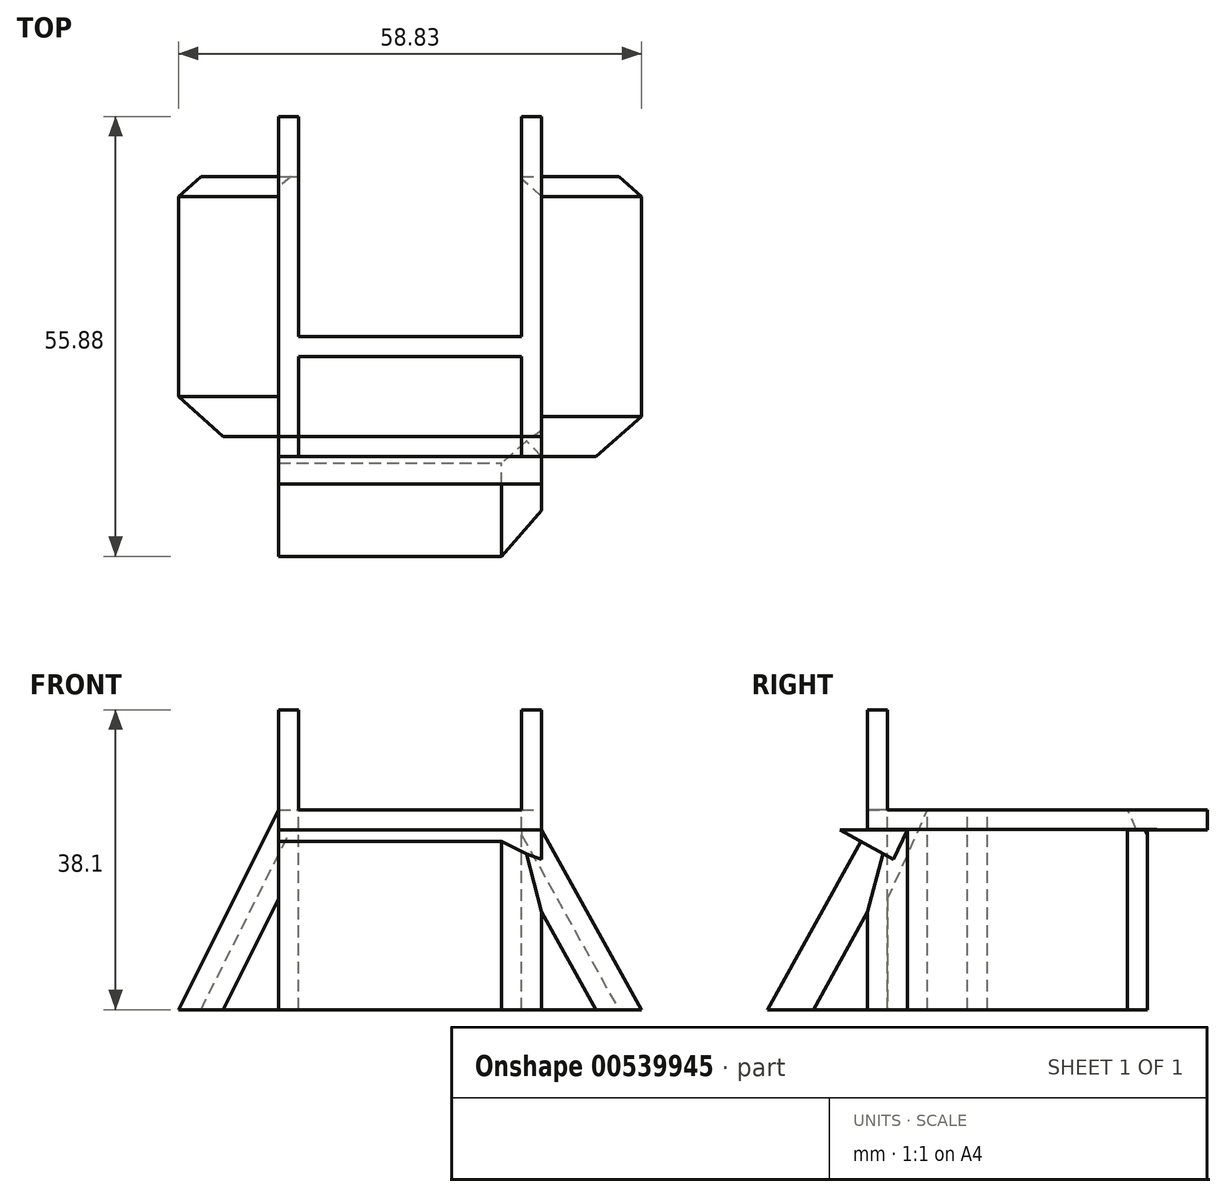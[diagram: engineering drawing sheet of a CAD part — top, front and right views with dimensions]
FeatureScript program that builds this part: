
annotation { "Feature Type Name" : "Feature", "Feature Type Description" : "" }
export const myFeature = defineFeature(function(context is Context, id is Id, definition is map)
    precondition{}
    {
        {
            var Q0;
            Q0=qCreatedBy(makeId("Front.planeOp"),FACE);
            var sketch = newSketch(context, id + "F0", { "sketchPlane" : qUnion([Q0])});
            skLineSegment(sketch, "E0.bottom", {"start": v(0, 0) * mm, "end": v(2.54, 0) * mm});
            skLineSegment(sketch, "E0.top", {"start": v(0, 2.54) * mm, "end": v(2.54, 2.54) * mm});
            skLineSegment(sketch, "E0.left", {"start": v(0, 0) * mm, "end": v(0, 2.54) * mm});
            skLineSegment(sketch, "E0.right", {"start": v(2.54, 0) * mm, "end": v(2.54, 2.54) * mm});
            skLineSegment(sketch, "E1", {"start": v(2.54, 0) * mm, "end": v(30.89, 0) * mm, "construction": true});
            skLineSegment(sketch, "E2.bottom", {"start": v(30.89, 0) * mm, "end": v(33.43, 0) * mm});
            skLineSegment(sketch, "E2.top", {"start": v(30.89, 2.54) * mm, "end": v(33.43, 2.54) * mm});
            skLineSegment(sketch, "E2.left", {"start": v(30.89, 0) * mm, "end": v(30.89, 2.54) * mm});
            skLineSegment(sketch, "E2.right", {"start": v(33.43, 0) * mm, "end": v(33.43, 2.54) * mm});
            skLineSegment(sketch, "E3.bottom", {"start": v(0, 0) * mm, "end": v(33.43, 0) * mm});
            skLineSegment(sketch, "E3.top", {"start": v(0, 2.54) * mm, "end": v(33.43, 2.54) * mm});
            skSolve(sketch);
        }
        {
            var Q0;
            {var subQ0=sQuery(id+"F0.wireOp",EDGE,"E0.right");Q0=makeQuery(id+"F0.imprint","IMPRINT",FACE,{"disambiguationData":[TD([[makeQuery(id+"F0.imprint","IMPRINT",EDGE,{"derivedFrom":subQ0}),-1.0]])]});}
            var Q1;
            {var subQ0=sQuery(id+"F0.wireOp",EDGE,"E0.right");Q1=makeQuery(id+"F0.imprint","IMPRINT",FACE,{"disambiguationData":[TD([[makeQuery(id+"F0.imprint","IMPRINT",EDGE,{"derivedFrom":subQ0}),1.0]])]});}
            var Q2;
            {var subQ0=sQuery(id+"F0.wireOp",EDGE,"E2.left");Q2=makeQuery(id+"F0.imprint","IMPRINT",FACE,{"disambiguationData":[TD([[makeQuery(id+"F0.imprint","IMPRINT",EDGE,{"derivedFrom":subQ0}),-1.0]])]});}
            extrude(context, id + "F1", {"entities" : qUnion([Q0, Q1, Q2]), "depth" : 43.18 * mm, "offsetDistance" : 25.4 * mm});
        }
        {
            var Q0;
            Q0=makeQuery(id+"F1.opExtrude","SWEPT_FACE",FACE,{"disambiguationData":[OSD([sQuery(id+"F0.wireOp",EDGE,"E3.top")])]});
            var sketch = newSketch(context, id + "F2", { "sketchPlane" : qUnion([Q0])});
            skLineSegment(sketch, "E4", {"start": v(0, 0) * mm, "end": v(2.54, 0) * mm});
            skLineSegment(sketch, "E5", {"start": v(2.54, 0) * mm, "end": v(30.89, 0) * mm, "construction": true});
            skLineSegment(sketch, "E6", {"start": v(30.89, 0) * mm, "end": v(33.43, 0) * mm});
            skLineSegment(sketch, "E7.bottom", {"start": v(2.54, 0) * mm, "end": v(30.89, 0) * mm});
            skLineSegment(sketch, "E7.top", {"start": v(2.54, -40.64) * mm, "end": v(30.89, -40.64) * mm});
            skLineSegment(sketch, "E7.left", {"start": v(2.54, 0) * mm, "end": v(2.54, -40.64) * mm});
            skLineSegment(sketch, "E7.right", {"start": v(30.89, 0) * mm, "end": v(30.89, -40.64) * mm});
            skLineSegment(sketch, "E8.bottom", {"start": v(2.54, -40.64) * mm, "end": v(0, -40.64) * mm});
            skLineSegment(sketch, "E8.top", {"start": v(2.54, -43.18) * mm, "end": v(0, -43.18) * mm});
            skLineSegment(sketch, "E8.left", {"start": v(2.54, -40.64) * mm, "end": v(2.54, -43.18) * mm});
            skLineSegment(sketch, "E8.right", {"start": v(0, -40.64) * mm, "end": v(0, -43.18) * mm});
            skLineSegment(sketch, "E9.bottom", {"start": v(30.89, -40.64) * mm, "end": v(33.43, -40.64) * mm});
            skLineSegment(sketch, "E9.top", {"start": v(30.89, -43.18) * mm, "end": v(33.43, -43.18) * mm});
            skLineSegment(sketch, "E9.left", {"start": v(30.89, -40.64) * mm, "end": v(30.89, -43.18) * mm});
            skLineSegment(sketch, "E9.right", {"start": v(33.43, -40.64) * mm, "end": v(33.43, -43.18) * mm});
            skLineSegment(sketch, "E10", {"start": v(2.54, 0) * mm, "end": v(2.54, -30.48) * mm, "construction": true});
            skLineSegment(sketch, "E11", {"start": v(2.54, -30.48) * mm, "end": v(30.89, -30.48) * mm});
            skLineSegment(sketch, "E12", {"start": v(2.54, -30.48) * mm, "end": v(2.54, -27.94) * mm});
            skLineSegment(sketch, "E13", {"start": v(2.54, -27.94) * mm, "end": v(30.89, -27.94) * mm});
            skLineSegment(sketch, "E14", {"start": v(0, 0) * mm, "end": v(0, -7.62) * mm});
            skLineSegment(sketch, "E15", {"start": v(0, -7.62) * mm, "end": v(2.54, -7.62) * mm});
            skLineSegment(sketch, "E16", {"start": v(33.43, 0) * mm, "end": v(33.43, -7.62) * mm});
            skLineSegment(sketch, "E17", {"start": v(33.43, -7.62) * mm, "end": v(30.89, -7.62) * mm});
            skSolve(sketch);
        }
        {
            var Q0;
            Q0=makeQuery(id+"F2.imprint","IMPRINT",FACE,{"disambiguationData":[TD([[makeQuery(id+"F2.imprint","IMPRINT",EDGE,{"derivedFrom":sQuery(id+"F2.wireOp",EDGE,"E7.bottom")}),-1.0]])]});
            var Q1;
            {var subQ0=sQuery(id+"F2.wireOp",EDGE,"E7.top");Q1=makeQuery(id+"F2.imprint","IMPRINT",FACE,{"disambiguationData":[TD([[makeQuery(id+"F2.imprint","IMPRINT",EDGE,{"derivedFrom":subQ0}),1.0]])]});}
            extrude(context, id + "F3", {"entities" : qUnion([Q0, Q1]), "operationType" : NewBodyOperationType.REMOVE, "oppositeDirection" : true, "depth" : 2.54 * mm, "offsetDistance" : 25.4 * mm});
        }
        {
            var Q0;
            Q0=makeQuery(id+"F2.imprint","IMPRINT",FACE,{"disambiguationData":[TD([[makeQuery(id+"F2.imprint","IMPRINT",EDGE,{"derivedFrom":sQuery(id+"F2.wireOp",EDGE,"E8.bottom")}),1.0]])]});
            var Q1;
            Q1=makeQuery(id+"F2.imprint","IMPRINT",FACE,{"disambiguationData":[TD([[makeQuery(id+"F2.imprint","IMPRINT",EDGE,{"derivedFrom":sQuery(id+"F2.wireOp",EDGE,"E9.bottom")}),-1.0]])]});
            extrude(context, id + "F4", {"entities" : qUnion([Q0, Q1]), "operationType" : NewBodyOperationType.ADD, "depth" : 12.7 * mm, "offsetDistance" : 25.4 * mm});
        }
        {
            var Q0;
            {var subQ0=sQuery(id+"F2.wireOp",EDGE,"E8.bottom");Q0=makeQuery(id+"F2.imprint","IMPRINT",FACE,{"disambiguationData":[TD([[makeQuery(id+"F2.imprint","IMPRINT",EDGE,{"derivedFrom":subQ0}),-1.0]])]});}
            var Q1;
            {var subQ0=sQuery(id+"F2.wireOp",EDGE,"E9.bottom");Q1=makeQuery(id+"F2.imprint","IMPRINT",FACE,{"disambiguationData":[TD([[makeQuery(id+"F2.imprint","IMPRINT",EDGE,{"derivedFrom":subQ0}),1.0]])]});}
            var Q2;
            Q2=makeQuery(id+"F2.imprint","IMPRINT",FACE,{"disambiguationData":[TD([[makeQuery(id+"F2.imprint","IMPRINT",EDGE,{"derivedFrom":sQuery(id+"F2.wireOp",EDGE,"E7.top")}),-1.0]])]});
            var Q3;
            Q3=makeQuery(id+"F2.imprint","IMPRINT",FACE,{"disambiguationData":[TD([[makeQuery(id+"F2.imprint","IMPRINT",EDGE,{"derivedFrom":sQuery(id+"F2.wireOp",EDGE,"E8.bottom")}),1.0]])]});
            var Q4;
            Q4=makeQuery(id+"F2.imprint","IMPRINT",FACE,{"disambiguationData":[TD([[makeQuery(id+"F2.imprint","IMPRINT",EDGE,{"derivedFrom":sQuery(id+"F2.wireOp",EDGE,"E9.bottom")}),-1.0]])]});
            extrude(context, id + "F5", {"entities" : qUnion([Q0, Q1, Q2, Q3, Q4]), "operationType" : NewBodyOperationType.ADD, "oppositeDirection" : true, "depth" : 25.4 * mm, "offsetDistance" : 25.4 * mm});
        }
        {
            var Q0;
            {var subQ0=sQuery(id+"F2.wireOp",EDGE,"E9.top");var subQ1=sQuery(id+"F2.wireOp",EDGE,"E8.top");var subQ2=sQuery(id+"F0.wireOp",EDGE,"E3.top");Q0=makeQuery(id+"F5.boolean.opBoolean","MERGE",FACE,{"derivedFrom":[makeQuery(id+"F4.boolean.opBoolean","MERGE",FACE,{"derivedFrom":[makeQuery(id+"F1.opExtrude","CAP_FACE",FACE,{"disambiguationData":[OSD([sQuery(id+"F0.wireOp",EDGE,"E3.bottom"),subQ2,sQuery(id+"F0.wireOp",EDGE,"E0.left"),sQuery(id+"F0.wireOp",EDGE,"E2.right")])],"isStart":false}),makeQuery(id+"F4.opExtrude","SWEPT_FACE",FACE,{"disambiguationData":[OSD([subQ1])]}),makeQuery(id+"F4.opExtrude","SWEPT_FACE",FACE,{"disambiguationData":[OSD([subQ0])]})]}),makeQuery(id+"F5.opExtrude","SWEPT_FACE",FACE,{"disambiguationData":[OSD([subQ2,subQ1,subQ0])]})]});}
            var sketch = newSketch(context, id + "F6", { "sketchPlane" : qUnion([Q0])});
            skLineSegment(sketch, "E18.bottom", {"start": v(0, 0) * mm, "end": v(33.43, 0) * mm});
            skLineSegment(sketch, "E18.top", {"start": v(0, -22.86) * mm, "end": v(33.43, -22.86) * mm});
            skLineSegment(sketch, "E18.left", {"start": v(0, 0) * mm, "end": v(0, -22.86) * mm});
            skLineSegment(sketch, "E18.right", {"start": v(33.43, 0) * mm, "end": v(33.43, -22.86) * mm});
            skSolve(sketch);
        }
        {
            var Q0;
            Q0=makeQuery(id+"F6.imprint","IMPRINT",FACE,{"disambiguationData":[TD([[makeQuery(id+"F6.imprint","IMPRINT",EDGE,{"derivedFrom":sQuery(id+"F6.wireOp",EDGE,"E18.bottom")}),-1.0]])]});
            extrude(context, id + "F7", {"entities" : qUnion([Q0]), "operationType" : NewBodyOperationType.ADD, "depth" : 12.7 * mm, "offsetDistance" : 25.4 * mm});
        }
        {
            var Q0;
            Q0=makeQuery(id+"F7.opExtrude","CAP_VERTEX",VERTEX,{"disambiguationData":[OSD([sQuery(id+"F0.wireOp",EDGE,"E0.left"),sQuery(id+"F2.wireOp",EDGE,"E8.top"),sQuery(id+"F2.wireOp",EDGE,"E8.right"),sQuery(id+"F6.wireOp",EDGE,"E18.bottom"),sQuery(id+"F6.wireOp",EDGE,"E18.left")])],"isStart":true});
            var Q1;
            Q1=makeQuery(id+"F7.opExtrude","CAP_VERTEX",VERTEX,{"disambiguationData":[OSD([sQuery(id+"F6.wireOp",EDGE,"E18.top"),sQuery(id+"F6.wireOp",EDGE,"E18.left")])],"isStart":false});
            var Q2;
            Q2=makeQuery(id+"F7.opExtrude","CAP_VERTEX",VERTEX,{"disambiguationData":[OSD([sQuery(id+"F6.wireOp",EDGE,"E18.top"),sQuery(id+"F6.wireOp",EDGE,"E18.right")])],"isStart":false});
            cPlane(context, id + "F8", {"entities" : qUnion([Q0, Q1, Q2]), "cplaneType" : CPlaneType.THREE_POINT, "offset" : 25.4 * mm, "width" : 152.4 * mm, "height" : 152.4 * mm});
        }
        {
            var Q0;
            Q0=qCreatedBy(id+"F8.planeOp",FACE);
            var sketch = newSketch(context, id + "F9", { "sketchPlane" : qUnion([Q0])});
            skLineSegment(sketch, "E19.bottom", {"start": v(0, -22.7) * mm, "end": v(-35.56, -22.7) * mm});
            skLineSegment(sketch, "E19.top", {"start": v(0, -50.64) * mm, "end": v(-35.56, -50.64) * mm});
            skLineSegment(sketch, "E19.left", {"start": v(0, -22.7) * mm, "end": v(0, -50.64) * mm});
            skLineSegment(sketch, "E19.right", {"start": v(-35.56, -22.7) * mm, "end": v(-35.56, -50.64) * mm});
            skSolve(sketch);
        }
        {
            var Q0;
            Q0=makeQuery(id+"F9.imprint","IMPRINT",FACE,{"disambiguationData":[TD([[makeQuery(id+"F9.imprint","IMPRINT",EDGE,{"derivedFrom":sQuery(id+"F9.wireOp",EDGE,"E19.bottom")}),1.0]])]});
            extrude(context, id + "F10", {"entities" : qUnion([Q0]), "operationType" : NewBodyOperationType.REMOVE, "oppositeDirection" : true, "depth" : 25.4 * mm, "offsetDistance" : 25.4 * mm});
        }
        {
            var Q0;
            {var subQ0=sQuery(id+"F2.wireOp",EDGE,"E9.right");var subQ1=sQuery(id+"F0.wireOp",EDGE,"E2.right");Q0=makeQuery(id+"F7.boolean.opBoolean","MERGE",FACE,{"derivedFrom":[makeQuery(id+"F5.boolean.opBoolean","MERGE",FACE,{"derivedFrom":[makeQuery(id+"F4.boolean.opBoolean","MERGE",FACE,{"derivedFrom":[makeQuery(id+"F1.opExtrude","SWEPT_FACE",FACE,{"disambiguationData":[OSD([subQ1])]}),makeQuery(id+"F4.opExtrude","SWEPT_FACE",FACE,{"disambiguationData":[OSD([subQ0])]})]}),makeQuery(id+"F5.opExtrude","SWEPT_FACE",FACE,{"disambiguationData":[OSD([sQuery(id+"F0.wireOp",EDGE,"E3.top"),subQ1,subQ0])]})]}),makeQuery(id+"F7.opExtrude","SWEPT_FACE",FACE,{"disambiguationData":[OSD([sQuery(id+"F6.wireOp",EDGE,"E18.right")])]})]});}
            var sketch = newSketch(context, id + "F11", { "sketchPlane" : qUnion([Q0])});
            skLineSegment(sketch, "E20.bottom", {"start": v(-43.18, 0) * mm, "end": v(-7.62, 0) * mm});
            skLineSegment(sketch, "E20.top", {"start": v(-43.18, -22.86) * mm, "end": v(-7.62, -22.86) * mm});
            skLineSegment(sketch, "E20.left", {"start": v(-43.18, 0) * mm, "end": v(-43.18, -22.86) * mm});
            skLineSegment(sketch, "E20.right", {"start": v(-7.62, 0) * mm, "end": v(-7.62, -22.86) * mm});
            skSolve(sketch);
        }
        {
            var Q0;
            Q0=makeQuery(id+"F11.imprint","IMPRINT",FACE,{"disambiguationData":[TD([[makeQuery(id+"F11.imprint","IMPRINT",EDGE,{"derivedFrom":sQuery(id+"F11.wireOp",EDGE,"E20.bottom")}),-1.0]])]});
            extrude(context, id + "F12", {"entities" : qUnion([Q0]), "operationType" : NewBodyOperationType.ADD, "depth" : 12.7 * mm, "offsetDistance" : 25.4 * mm});
        }
        {
            var Q0;
            {var subQ0=sQuery(id+"F6.wireOp",EDGE,"E18.right");var subQ1=sQuery(id+"F6.wireOp",EDGE,"E18.bottom");var subQ2=sQuery(id+"F2.wireOp",EDGE,"E9.right");var subQ3=sQuery(id+"F2.wireOp",EDGE,"E9.top");var subQ4=sQuery(id+"F0.wireOp",EDGE,"E2.right");Q0=makeQuery(id+"F12.boolean.opBoolean","MERGE",VERTEX,{"derivedFrom":[makeQuery(id+"F7.opExtrude","CAP_VERTEX",VERTEX,{"disambiguationData":[OSD([subQ4,subQ3,subQ2,subQ1,subQ0])],"isStart":true}),makeQuery(id+"F12.opExtrude","CAP_VERTEX",VERTEX,{"disambiguationData":[OSD([subQ4,subQ3,subQ2,subQ1,subQ0,sQuery(id+"F11.wireOp",EDGE,"E20.bottom"),sQuery(id+"F11.wireOp",EDGE,"E20.left")])],"isStart":true})]});}
            var Q1;
            Q1=makeQuery(id+"F12.opExtrude","CAP_VERTEX",VERTEX,{"disambiguationData":[OSD([sQuery(id+"F0.wireOp",EDGE,"E3.top"),sQuery(id+"F0.wireOp",EDGE,"E2.right"),sQuery(id+"F2.wireOp",EDGE,"E9.right"),sQuery(id+"F6.wireOp",EDGE,"E18.top"),sQuery(id+"F6.wireOp",EDGE,"E18.right"),sQuery(id+"F11.wireOp",EDGE,"E20.top"),sQuery(id+"F11.wireOp",EDGE,"E20.left")])],"isStart":false});
            var Q2;
            Q2=makeQuery(id+"F12.opExtrude","CAP_VERTEX",VERTEX,{"disambiguationData":[OSD([sQuery(id+"F11.wireOp",EDGE,"E20.top"),sQuery(id+"F11.wireOp",EDGE,"E20.right")])],"isStart":false});
            cPlane(context, id + "F13", {"entities" : qUnion([Q0, Q1, Q2]), "cplaneType" : CPlaneType.THREE_POINT, "offset" : 25.4 * mm, "width" : 152.4 * mm, "height" : 152.4 * mm});
        }
        {
            var Q0;
            Q0=qCreatedBy(id+"F13.planeOp",FACE);
            var sketch = newSketch(context, id + "F14", { "sketchPlane" : qUnion([Q0])});
            skLineSegment(sketch, "E21.bottom", {"start": v(43.26, -16.18) * mm, "end": v(6.43, -16.18) * mm});
            skLineSegment(sketch, "E21.top", {"start": v(43.26, -44.3) * mm, "end": v(6.43, -44.3) * mm});
            skLineSegment(sketch, "E21.left", {"start": v(43.26, -16.18) * mm, "end": v(43.26, -44.3) * mm});
            skLineSegment(sketch, "E21.right", {"start": v(6.43, -16.18) * mm, "end": v(6.43, -44.3) * mm});
            skSolve(sketch);
        }
        {
            var Q0;
            Q0=makeQuery(id+"F14.imprint","IMPRINT",FACE,{"disambiguationData":[TD([[makeQuery(id+"F14.imprint","IMPRINT",EDGE,{"derivedFrom":sQuery(id+"F14.wireOp",EDGE,"E21.bottom")}),1.0]])]});
            extrude(context, id + "F15", {"entities" : qUnion([Q0]), "operationType" : NewBodyOperationType.REMOVE, "oppositeDirection" : true, "depth" : 25.4 * mm, "offsetDistance" : 25.4 * mm});
        }
        {
            var Q0;
            {var subQ0=sQuery(id+"F2.wireOp",EDGE,"E8.right");var subQ1=sQuery(id+"F0.wireOp",EDGE,"E0.left");Q0=makeQuery(id+"F7.boolean.opBoolean","MERGE",FACE,{"derivedFrom":[makeQuery(id+"F5.boolean.opBoolean","MERGE",FACE,{"derivedFrom":[makeQuery(id+"F4.boolean.opBoolean","MERGE",FACE,{"derivedFrom":[makeQuery(id+"F1.opExtrude","SWEPT_FACE",FACE,{"disambiguationData":[OSD([subQ1])]}),makeQuery(id+"F4.opExtrude","SWEPT_FACE",FACE,{"disambiguationData":[OSD([subQ0])]})]}),makeQuery(id+"F5.opExtrude","SWEPT_FACE",FACE,{"disambiguationData":[OSD([sQuery(id+"F0.wireOp",EDGE,"E3.top"),subQ1,subQ0])]})]}),makeQuery(id+"F7.opExtrude","SWEPT_FACE",FACE,{"disambiguationData":[OSD([sQuery(id+"F6.wireOp",EDGE,"E18.left")])]})]});}
            var sketch = newSketch(context, id + "F16", { "sketchPlane" : qUnion([Q0])});
            skLineSegment(sketch, "E22.bottom", {"start": v(40.64, 2.54) * mm, "end": v(7.62, 2.54) * mm});
            skLineSegment(sketch, "E22.top", {"start": v(40.64, -22.86) * mm, "end": v(7.62, -22.86) * mm});
            skLineSegment(sketch, "E22.left", {"start": v(40.64, 2.54) * mm, "end": v(40.64, -22.86) * mm});
            skLineSegment(sketch, "E22.right", {"start": v(7.62, 2.54) * mm, "end": v(7.62, -22.86) * mm});
            skSolve(sketch);
        }
        {
            var Q0;
            {var subQ3=sQuery(id+"F16.wireOp",EDGE,"E22.bottom");Q0=makeQuery(id+"F16.imprint","IMPRINT",FACE,{"disambiguationData":[TD([[makeQuery(id+"F16.imprint","IMPRINT",EDGE,{"derivedFrom":subQ3}),1.0]])]});}
            extrude(context, id + "F17", {"entities" : qUnion([Q0]), "operationType" : NewBodyOperationType.ADD, "depth" : 12.7 * mm, "offsetDistance" : 25.4 * mm});
        }
        {
            var Q0;
            Q0=makeQuery(id+"F17.opExtrude","CAP_VERTEX",VERTEX,{"disambiguationData":[OSD([sQuery(id+"F0.wireOp",EDGE,"E3.top"),sQuery(id+"F0.wireOp",EDGE,"E0.left"),sQuery(id+"F16.wireOp",EDGE,"E22.bottom"),sQuery(id+"F16.wireOp",EDGE,"E22.right")])],"isStart":true});
            var Q1;
            Q1=makeQuery(id+"F17.opExtrude","CAP_VERTEX",VERTEX,{"disambiguationData":[OSD([sQuery(id+"F0.wireOp",EDGE,"E3.top"),sQuery(id+"F0.wireOp",EDGE,"E0.left"),sQuery(id+"F2.wireOp",EDGE,"E8.right"),sQuery(id+"F6.wireOp",EDGE,"E18.top"),sQuery(id+"F6.wireOp",EDGE,"E18.left"),sQuery(id+"F16.wireOp",EDGE,"E22.top"),sQuery(id+"F16.wireOp",EDGE,"E22.left")])],"isStart":false});
            var Q2;
            Q2=makeQuery(id+"F17.opExtrude","CAP_VERTEX",VERTEX,{"disambiguationData":[OSD([sQuery(id+"F16.wireOp",EDGE,"E22.top"),sQuery(id+"F16.wireOp",EDGE,"E22.right")])],"isStart":false});
            cPlane(context, id + "F18", {"entities" : qUnion([Q0, Q1, Q2]), "cplaneType" : CPlaneType.THREE_POINT, "offset" : 25.4 * mm, "width" : 152.4 * mm, "height" : 152.4 * mm});
        }
        {
            var Q0;
            Q0=qCreatedBy(id+"F18.planeOp",FACE);
            var sketch = newSketch(context, id + "F19", { "sketchPlane" : qUnion([Q0])});
            skLineSegment(sketch, "E23.bottom", {"start": v(7.38, 2.28) * mm, "end": v(43.71, 2.28) * mm});
            skLineSegment(sketch, "E23.top", {"start": v(7.38, -36.42) * mm, "end": v(43.71, -36.42) * mm});
            skLineSegment(sketch, "E23.left", {"start": v(7.38, 2.28) * mm, "end": v(7.38, -36.42) * mm});
            skLineSegment(sketch, "E23.right", {"start": v(43.71, 2.28) * mm, "end": v(43.71, -36.42) * mm});
            skSolve(sketch);
        }
        {
            var Q0;
            Q0=makeQuery(id+"F19.imprint","IMPRINT",FACE,{"disambiguationData":[TD([[makeQuery(id+"F19.imprint","IMPRINT",EDGE,{"derivedFrom":sQuery(id+"F19.wireOp",EDGE,"E23.bottom")}),-1.0]])]});
            extrude(context, id + "F20", {"entities" : qUnion([Q0]), "operationType" : NewBodyOperationType.REMOVE, "depth" : 25.4 * mm, "offsetDistance" : 25.4 * mm});
        }
        {
            var Q0;
            Q0=makeQuery(id+"F10.boolean.opBoolean","COPY",EDGE,{"derivedFrom":makeQuery(id+"F10.opExtrude","CAP_EDGE",EDGE,{"disambiguationData":[OSD([sQuery(id+"F9.wireOp",EDGE,"E19.left")])],"isStart":true})});
            var Q1;
            {var subQ0=sQuery(id+"F2.wireOp",EDGE,"E9.right");var subQ1=sQuery(id+"F0.wireOp",EDGE,"E2.right");Q1=makeQuery(id+"F10.boolean.opBoolean","INTERSECT",EDGE,{"derivedFrom":[makeQuery(id+"F7.boolean.opBoolean","MERGE",FACE,{"derivedFrom":[makeQuery(id+"F5.boolean.opBoolean","MERGE",FACE,{"derivedFrom":[makeQuery(id+"F4.boolean.opBoolean","MERGE",FACE,{"derivedFrom":[makeQuery(id+"F1.opExtrude","SWEPT_FACE",FACE,{"disambiguationData":[OSD([subQ1])]}),makeQuery(id+"F4.opExtrude","SWEPT_FACE",FACE,{"disambiguationData":[OSD([subQ0])]})]}),makeQuery(id+"F5.opExtrude","SWEPT_FACE",FACE,{"disambiguationData":[OSD([sQuery(id+"F0.wireOp",EDGE,"E3.top"),subQ1,subQ0])]})]}),makeQuery(id+"F7.opExtrude","SWEPT_FACE",FACE,{"disambiguationData":[OSD([sQuery(id+"F6.wireOp",EDGE,"E18.right")])]})]}),makeQuery(id+"F10.opExtrude","CAP_FACE",FACE,{"disambiguationData":[OSD([sQuery(id+"F9.wireOp",EDGE,"E19.bottom"),sQuery(id+"F9.wireOp",EDGE,"E19.top"),sQuery(id+"F9.wireOp",EDGE,"E19.left"),sQuery(id+"F9.wireOp",EDGE,"E19.right")])],"isStart":true})]});}
            chamfer(context, id + "F21", {"entities" : qUnion([Q0, Q1]), "width" : 5.08 * mm, "tangentPropagation" : true});
        }
        {
            var Q0;
            Q0=makeQuery(id+"F20.boolean.opBoolean","INTERSECT",EDGE,{"derivedFrom":[makeQuery(id+"F17.opExtrude","SWEPT_FACE",FACE,{"disambiguationData":[OSD([sQuery(id+"F16.wireOp",EDGE,"E22.left")])]}),makeQuery(id+"F20.opExtrude","CAP_FACE",FACE,{"disambiguationData":[OSD([sQuery(id+"F19.wireOp",EDGE,"E23.bottom"),sQuery(id+"F19.wireOp",EDGE,"E23.top"),sQuery(id+"F19.wireOp",EDGE,"E23.left"),sQuery(id+"F19.wireOp",EDGE,"E23.right")])],"isStart":true})]});
            var Q1;
            Q1=makeQuery(id+"F15.boolean.opBoolean","INTERSECT",EDGE,{"derivedFrom":[makeQuery(id+"F12.opExtrude","SWEPT_FACE",FACE,{"disambiguationData":[OSD([sQuery(id+"F11.wireOp",EDGE,"E20.left")])]}),makeQuery(id+"F15.opExtrude","CAP_FACE",FACE,{"disambiguationData":[OSD([sQuery(id+"F14.wireOp",EDGE,"E21.bottom"),sQuery(id+"F14.wireOp",EDGE,"E21.top"),sQuery(id+"F14.wireOp",EDGE,"E21.left"),sQuery(id+"F14.wireOp",EDGE,"E21.right")])],"isStart":true})]});
            chamfer(context, id + "F22", {"entities" : qUnion([Q0, Q1]), "width" : 5.08 * mm, "tangentPropagation" : true});
        }
        {
            var Q0;
            Q0=makeQuery(id+"F20.boolean.opBoolean","INTERSECT",EDGE,{"derivedFrom":[makeQuery(id+"F17.boolean.opBoolean","MERGE",FACE,{"derivedFrom":[makeQuery(id+"F5.opExtrude","SWEPT_FACE",FACE,{"disambiguationData":[OSD([sQuery(id+"F2.wireOp",EDGE,"E15")])]}),makeQuery(id+"F17.opExtrude","SWEPT_FACE",FACE,{"disambiguationData":[OSD([sQuery(id+"F16.wireOp",EDGE,"E22.right")])]})]}),makeQuery(id+"F20.opExtrude","CAP_FACE",FACE,{"disambiguationData":[OSD([sQuery(id+"F19.wireOp",EDGE,"E23.bottom"),sQuery(id+"F19.wireOp",EDGE,"E23.top"),sQuery(id+"F19.wireOp",EDGE,"E23.left"),sQuery(id+"F19.wireOp",EDGE,"E23.right")])],"isStart":true})]});
            var Q1;
            Q1=makeQuery(id+"F15.boolean.opBoolean","INTERSECT",EDGE,{"derivedFrom":[makeQuery(id+"F12.boolean.opBoolean","MERGE",FACE,{"derivedFrom":[makeQuery(id+"F5.opExtrude","SWEPT_FACE",FACE,{"disambiguationData":[OSD([sQuery(id+"F2.wireOp",EDGE,"E17")])]}),makeQuery(id+"F12.opExtrude","SWEPT_FACE",FACE,{"disambiguationData":[OSD([sQuery(id+"F11.wireOp",EDGE,"E20.right")])]})]}),makeQuery(id+"F15.opExtrude","CAP_FACE",FACE,{"disambiguationData":[OSD([sQuery(id+"F14.wireOp",EDGE,"E21.bottom"),sQuery(id+"F14.wireOp",EDGE,"E21.top"),sQuery(id+"F14.wireOp",EDGE,"E21.left"),sQuery(id+"F14.wireOp",EDGE,"E21.right")])],"isStart":true})]});
            chamfer(context, id + "F23", {"entities" : qUnion([Q0, Q1]), "width" : 2.54 * mm, "tangentPropagation" : true});
        }
        {
            var Q0;
            {var subQ14=sQuery(id+"F0.wireOp",EDGE,"E0.left");var subQ15=sQuery(id+"F0.wireOp",EDGE,"E3.top");var subQ16=makeQuery(id+"F1.opExtrude","SWEPT_FACE",FACE,{"disambiguationData":[OSD([subQ15])]});Q0=makeQuery(id+"F17.boolean.opBoolean","MERGE",FACE,{"derivedFrom":[makeQuery(id+"F4.boolean.opBoolean","SPLIT",FACE,{"disambiguationData":[TD([makeQuery(id+"F1.opExtrude","SWEPT_FACE",FACE,{"disambiguationData":[OSD([subQ14])]})])],"derivedFrom":subQ16}),makeQuery(id+"F17.opExtrude","SWEPT_FACE",FACE,{"disambiguationData":[OSD([sQuery(id+"F16.wireOp",EDGE,"E22.bottom")])]})]});}
            var sketch = newSketch(context, id + "F24", { "sketchPlane" : qUnion([Q0])});
            skLineSegment(sketch, "E24.bottom", {"start": v(2.54, -30.48) * mm, "end": v(30.89, -30.48) * mm});
            skLineSegment(sketch, "E24.top", {"start": v(2.54, -27.94) * mm, "end": v(30.89, -27.94) * mm});
            skLineSegment(sketch, "E24.left", {"start": v(2.54, -30.48) * mm, "end": v(2.54, -27.94) * mm});
            skLineSegment(sketch, "E24.right", {"start": v(30.89, -30.48) * mm, "end": v(30.89, -27.94) * mm});
            skSolve(sketch);
        }
        {
            var Q0;
            Q0 = qSketchRegion(id + "F24", true);
            extrude(context, id + "F25", {"entities" : qUnion([Q0]), "operationType" : NewBodyOperationType.ADD, "oppositeDirection" : true, "depth" : 25.4 * mm, "offsetDistance" : 25.4 * mm});
        }
    });
